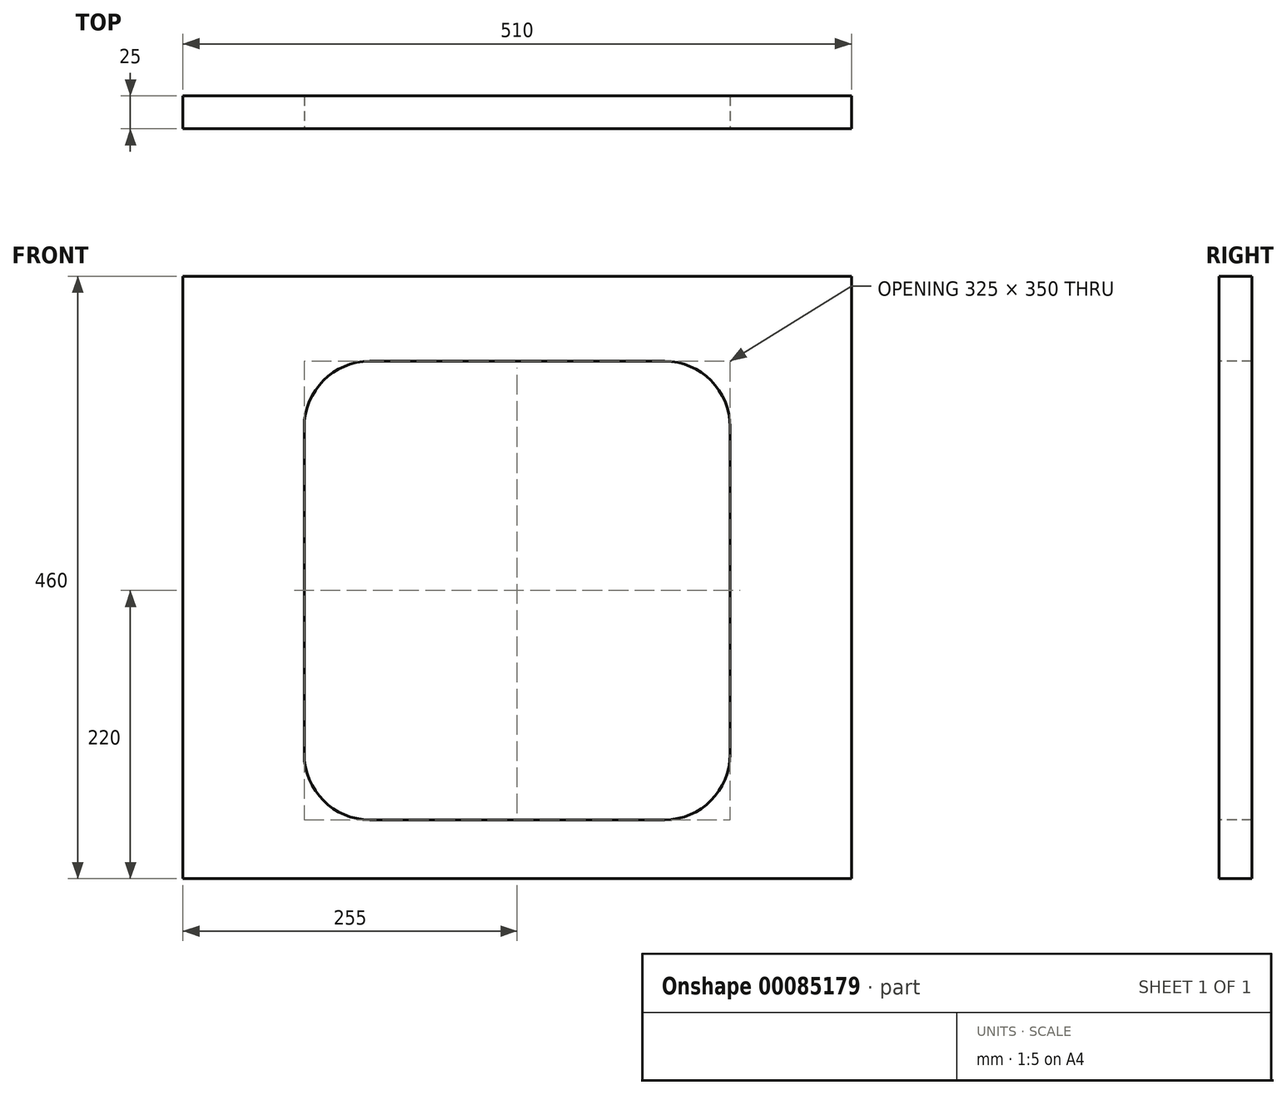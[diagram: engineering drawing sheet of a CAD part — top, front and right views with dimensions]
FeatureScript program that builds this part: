
annotation { "Feature Type Name" : "Feature", "Feature Type Description" : "" }
export const myFeature = defineFeature(function(context is Context, id is Id, definition is map)
    precondition{}
    {
        {
            var Q0;
            Q0=qCreatedBy(makeId("Front.planeOp"),FACE);
            var sketch = newSketch(context, id + "F0", { "sketchPlane" : qUnion([Q0])});
            skLineSegment(sketch, "E0.bottom", {"start": v(255, -230) * mm, "end": v(-255, -230) * mm});
            skLineSegment(sketch, "E0.top", {"start": v(255, 230) * mm, "end": v(-255, 230) * mm});
            skLineSegment(sketch, "E0.left", {"start": v(255, -230) * mm, "end": v(255, 230) * mm});
            skLineSegment(sketch, "E0.right", {"start": v(-255, -230) * mm, "end": v(-255, 230) * mm});
            skPoint(sketch, "E0.middle", {"position": v(0, 0) * mm});
            skSolve(sketch);
        }
        {
            var Q0;
            Q0 = qSketchRegion(id + "F0", true);
            extrude(context, id + "F1", {"entities" : qUnion([Q0]), "depth" : 25 * mm});
        }
        {
            var Q0;
            Q0=makeQuery(id+"F1.opExtrude","CAP_FACE",FACE,{"disambiguationData":[OSD([sQuery(id+"F0.wireOp",EDGE,"E0.bottom"),sQuery(id+"F0.wireOp",EDGE,"E0.top"),sQuery(id+"F0.wireOp",EDGE,"E0.left"),sQuery(id+"F0.wireOp",EDGE,"E0.right")])],"isStart":false});
            var sketch = newSketch(context, id + "F2", { "sketchPlane" : qUnion([Q0])});
            skLineSegment(sketch, "E1.bottom", {"start": v(162.5, 165) * mm, "end": v(-162.5, 165) * mm});
            skLineSegment(sketch, "E1.top", {"start": v(162.5, -185) * mm, "end": v(-162.5, -185) * mm});
            skLineSegment(sketch, "E1.left", {"start": v(162.5, 165) * mm, "end": v(162.5, -185) * mm});
            skLineSegment(sketch, "E1.right", {"start": v(-162.5, 165) * mm, "end": v(-162.5, -185) * mm});
            skPoint(sketch, "E1.middle", {"position": v(0, -10) * mm});
            skSolve(sketch);
        }
        {
            var Q0;
            Q0 = qSketchRegion(id + "F2", true);
            extrude(context, id + "F3", {"entities" : qUnion([Q0]), "operationType" : NewBodyOperationType.REMOVE, "oppositeDirection" : true, "depth" : 25 * mm});
        }
        {
            var Q0;
            Q0=makeQuery(id+"F3.boolean.opBoolean","COPY",EDGE,{"derivedFrom":makeQuery(id+"F3.opExtrude","SWEPT_EDGE",EDGE,{"disambiguationData":[OSD([sQuery(id+"F2.wireOp",EDGE,"E1.bottom"),sQuery(id+"F2.wireOp",EDGE,"E1.right")])]})});
            var Q1;
            Q1=makeQuery(id+"F3.boolean.opBoolean","COPY",EDGE,{"derivedFrom":makeQuery(id+"F3.opExtrude","SWEPT_EDGE",EDGE,{"disambiguationData":[OSD([sQuery(id+"F2.wireOp",EDGE,"E1.bottom"),sQuery(id+"F2.wireOp",EDGE,"E1.left")])]})});
            var Q2;
            Q2=makeQuery(id+"F3.boolean.opBoolean","COPY",EDGE,{"derivedFrom":makeQuery(id+"F3.opExtrude","SWEPT_EDGE",EDGE,{"disambiguationData":[OSD([sQuery(id+"F2.wireOp",EDGE,"E1.top"),sQuery(id+"F2.wireOp",EDGE,"E1.right")])]})});
            var Q3;
            Q3=makeQuery(id+"F3.boolean.opBoolean","COPY",EDGE,{"derivedFrom":makeQuery(id+"F3.opExtrude","SWEPT_EDGE",EDGE,{"disambiguationData":[OSD([sQuery(id+"F2.wireOp",EDGE,"E1.top"),sQuery(id+"F2.wireOp",EDGE,"E1.left")])]})});
            fillet(context, id + "F4", {"entities" : qUnion([Q0, Q1, Q2, Q3]), "radius" : 50 * mm, "tangentPropagation" : true, "allowEdgeOverflow" : false});
        }
    });
